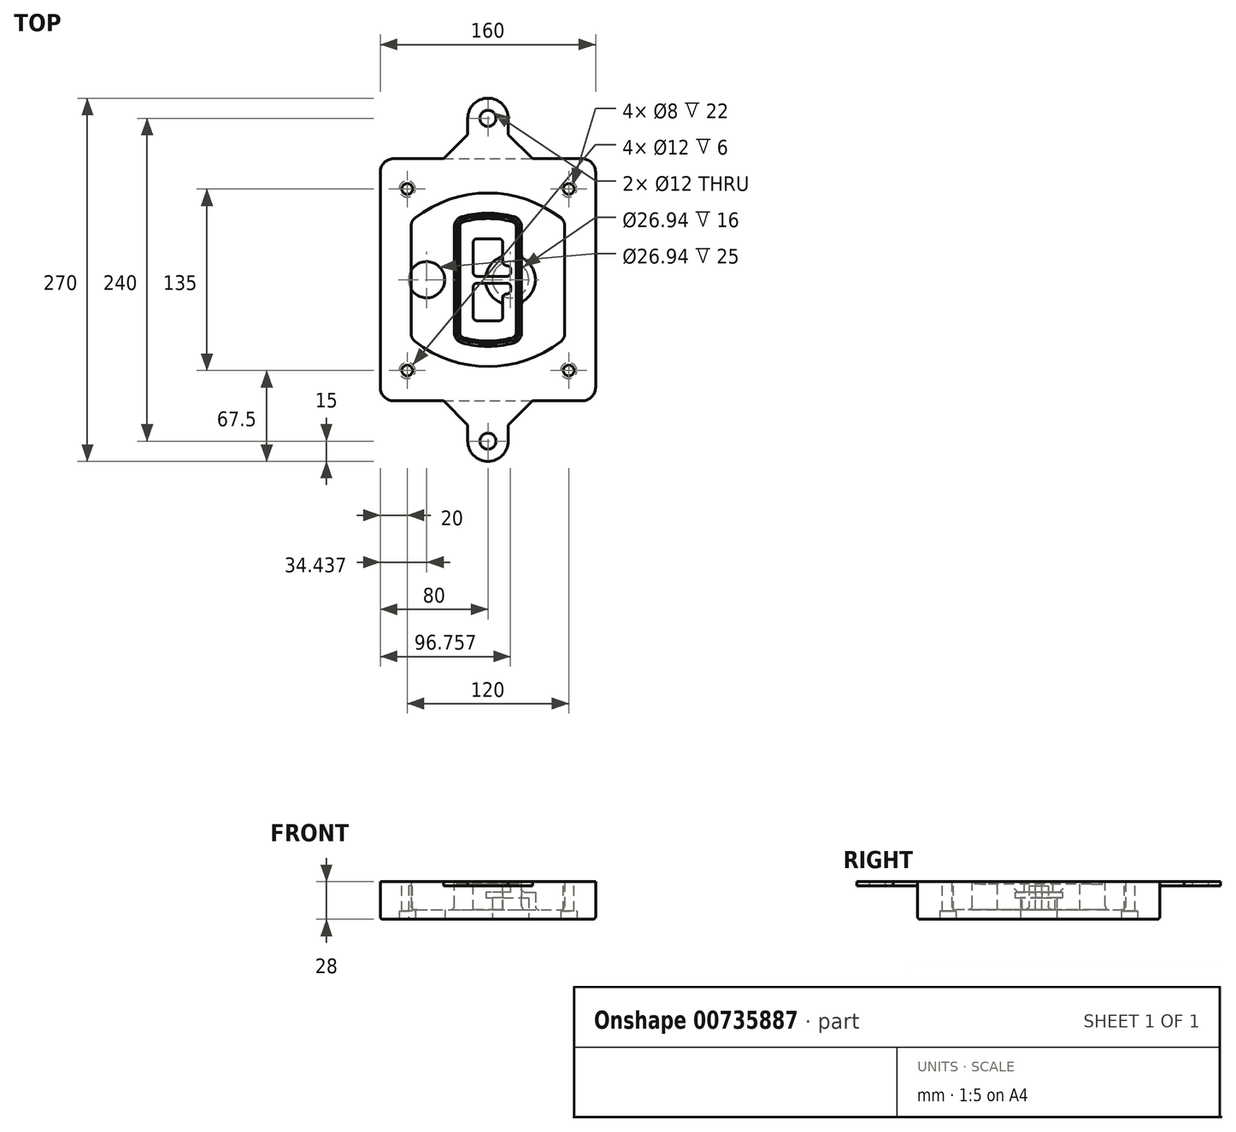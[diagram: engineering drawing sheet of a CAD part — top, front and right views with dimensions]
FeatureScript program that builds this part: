
annotation { "Feature Type Name" : "Feature", "Feature Type Description" : "" }
export const myFeature = defineFeature(function(context is Context, id is Id, definition is map)
    precondition{}
    {
        {
            var Q0;
            Q0=qCreatedBy(makeId("Top.planeOp"),FACE);
            var sketch = newSketch(context, id + "F0", { "sketchPlane" : qUnion([Q0])});
            skPoint(sketch, "E0.rect.middle", {"position": v(0, 0) * mm});
            skLineSegment(sketch, "E1.bottom", {"start": v(-70, -90) * mm, "end": v(70, -90) * mm});
            skLineSegment(sketch, "E1.top", {"start": v(-70, 90) * mm, "end": v(70, 90) * mm});
            skLineSegment(sketch, "E1.left", {"start": v(-80, -80) * mm, "end": v(-80, 80) * mm});
            skLineSegment(sketch, "E1.right", {"start": v(80, -80) * mm, "end": v(80, 80) * mm});
            skLineSegment(sketch, "E2", {"start": v(-80, 90) * mm, "end": v(80, -90) * mm, "construction": true});
            skLineSegment(sketch, "E3", {"start": v(80, 90) * mm, "end": v(-80, -90) * mm, "construction": true});
            skCircle(sketch, "E4", {"center": v(-60, 67.5) * mm, "radius": 4 * mm});
            skCircle(sketch, "E5", {"center": v(60, 67.5) * mm, "radius": 4 * mm});
            skCircle(sketch, "E6", {"center": v(60, -67.5) * mm, "radius": 4 * mm});
            skCircle(sketch, "E7", {"center": v(-60, -67.5) * mm, "radius": 4 * mm});
            skLineSegment(sketch, "E8", {"start": v(-60, 67.5) * mm, "end": v(60, 67.5) * mm, "construction": true});
            skLineSegment(sketch, "E9", {"start": v(60, 67.5) * mm, "end": v(60, -67.5) * mm, "construction": true});
            skLineSegment(sketch, "E10", {"start": v(60, -67.5) * mm, "end": v(-60, -67.5) * mm, "construction": true});
            skLineSegment(sketch, "E11", {"start": v(-60, -67.5) * mm, "end": v(-60, 67.5) * mm, "construction": true});
            skLineSegment(sketch, "E12", {"start": v(-60, 40.3) * mm, "end": v(-60, -40.3) * mm});
            skLineSegment(sketch, "E13", {"start": v(60, 40.3) * mm, "end": v(60, -40.3) * mm});
            skArc(sketch, "E14", {"start": v(56.15, 48.18) * mm, "mid": v(0, 67.5) * mm, "end": v(-56.15, 48.18) * mm});
            skArc(sketch, "E15", {"start": v(-56.15, -48.18) * mm, "mid": v(0, -67.5) * mm, "end": v(56.15, -48.18) * mm});
            skLineSegment(sketch, "E16", {"start": v(-60, 0) * mm, "end": v(60, 0) * mm, "construction": true});
            skPoint(sketch, "E17.visualSharp", {"position": v(-60, -45) * mm});
            skArc(sketch, "E17.filletArc", {"start": v(-60, -40.3) * mm, "mid": v(-58.99, -44.68) * mm, "end": v(-56.15, -48.18) * mm});
            skPoint(sketch, "E18.visualSharp", {"position": v(-60, 45) * mm});
            skArc(sketch, "E18.filletArc", {"start": v(-56.15, 48.18) * mm, "mid": v(-58.99, 44.68) * mm, "end": v(-60, 40.3) * mm});
            skPoint(sketch, "E19.visualSharp", {"position": v(60, 45) * mm});
            skArc(sketch, "E19.filletArc", {"start": v(60, 40.3) * mm, "mid": v(58.99, 44.68) * mm, "end": v(56.15, 48.18) * mm});
            skPoint(sketch, "E20.visualSharp", {"position": v(60, -45) * mm});
            skArc(sketch, "E20.filletArc", {"start": v(56.15, -48.18) * mm, "mid": v(58.99, -44.68) * mm, "end": v(60, -40.3) * mm});
            skPoint(sketch, "E21.visualSharp", {"position": v(-80, 90) * mm});
            skArc(sketch, "E21.filletArc", {"start": v(-70, 90) * mm, "mid": v(-77.07, 87.07) * mm, "end": v(-80, 80) * mm});
            skPoint(sketch, "E22.visualSharp", {"position": v(80, 90) * mm});
            skArc(sketch, "E22.filletArc", {"start": v(80, 80) * mm, "mid": v(77.07, 87.07) * mm, "end": v(70, 90) * mm});
            skPoint(sketch, "E23.visualSharp", {"position": v(80, -90) * mm});
            skArc(sketch, "E23.filletArc", {"start": v(70, -90) * mm, "mid": v(77.07, -87.07) * mm, "end": v(80, -80) * mm});
            skPoint(sketch, "E24.visualSharp", {"position": v(-80, -90) * mm});
            skArc(sketch, "E24.filletArc", {"start": v(-80, -80) * mm, "mid": v(-77.07, -87.07) * mm, "end": v(-70, -90) * mm});
            skArc(sketch, "E25.0", {"start": v(57, 40.3) * mm, "mid": v(56.3, 43.36) * mm, "end": v(54.3, 45.81) * mm});
            skLineSegment(sketch, "E25.1", {"start": v(57, 40.3) * mm, "end": v(57, -40.3) * mm});
            skArc(sketch, "E25.2", {"start": v(54.3, -45.81) * mm, "mid": v(56.3, -43.36) * mm, "end": v(57, -40.3) * mm});
            skArc(sketch, "E25.3", {"start": v(-54.3, -45.81) * mm, "mid": v(0, -64.5) * mm, "end": v(54.3, -45.81) * mm});
            skArc(sketch, "E25.4", {"start": v(-57, -40.3) * mm, "mid": v(-56.3, -43.36) * mm, "end": v(-54.3, -45.81) * mm});
            skArc(sketch, "E25.5", {"start": v(54.3, 45.81) * mm, "mid": v(0, 64.5) * mm, "end": v(-54.3, 45.81) * mm});
            skLineSegment(sketch, "E25.6", {"start": v(-57, 40.3) * mm, "end": v(-57, -40.3) * mm});
            skArc(sketch, "E25.7", {"start": v(-54.3, 45.81) * mm, "mid": v(-56.3, 43.36) * mm, "end": v(-57, 40.3) * mm});
            skArc(sketch, "E26.0", {"start": v(-58.62, 51.33) * mm, "mid": v(-62.58, 46.43) * mm, "end": v(-64, 40.3) * mm});
            skArc(sketch, "E26.1", {"start": v(58.62, 51.33) * mm, "mid": v(0, 71.5) * mm, "end": v(-58.62, 51.33) * mm});
            skArc(sketch, "E26.2", {"start": v(64, 40.3) * mm, "mid": v(62.58, 46.43) * mm, "end": v(58.62, 51.33) * mm});
            skLineSegment(sketch, "E26.3", {"start": v(64, 40.3) * mm, "end": v(64, -40.3) * mm});
            skArc(sketch, "E26.4", {"start": v(58.62, -51.33) * mm, "mid": v(62.58, -46.43) * mm, "end": v(64, -40.3) * mm});
            skLineSegment(sketch, "E26.5", {"start": v(-64, 40.3) * mm, "end": v(-64, -40.3) * mm});
            skArc(sketch, "E26.6", {"start": v(-58.62, -51.33) * mm, "mid": v(0, -71.5) * mm, "end": v(58.62, -51.33) * mm});
            skArc(sketch, "E26.7", {"start": v(-64, -40.3) * mm, "mid": v(-62.58, -46.43) * mm, "end": v(-58.62, -51.33) * mm});
            skSolve(sketch);
        }
        {
            var Q0;
            Q0=makeQuery(id+"F0.imprint","IMPRINT",FACE,{"disambiguationData":[TD([[makeQuery(id+"F0.imprint","IMPRINT",EDGE,{"derivedFrom":sQuery(id+"F0.wireOp",EDGE,"E1.bottom")}),1.0]])]});
            var Q1;
            Q1=makeQuery(id+"F0.imprint","IMPRINT",FACE,{"disambiguationData":[TD([[makeQuery(id+"F0.imprint","IMPRINT",EDGE,{"derivedFrom":sQuery(id+"F0.wireOp",EDGE,"E12")}),1.0]])]});
            var Q2;
            Q2=makeQuery(id+"F0.imprint","IMPRINT",FACE,{"disambiguationData":[TD([[makeQuery(id+"F0.imprint","IMPRINT",EDGE,{"derivedFrom":sQuery(id+"F0.wireOp",EDGE,"E25.0")}),1.0]])]});
            var Q3;
            Q3=makeQuery(id+"F0.imprint","IMPRINT",FACE,{"disambiguationData":[TD([[makeQuery(id+"F0.imprint","IMPRINT",EDGE,{"derivedFrom":sQuery(id+"F0.wireOp",EDGE,"E12")}),-1.0]])]});
            extrude(context, id + "F1", {"entities" : qUnion([Q0, Q1, Q2, Q3]), "oppositeDirection" : true, "depth" : 25 * mm});
        }
        {
            var Q0;
            Q0=makeQuery(id+"F0.imprint","IMPRINT",FACE,{"disambiguationData":[TD([[makeQuery(id+"F0.imprint","IMPRINT",EDGE,{"derivedFrom":sQuery(id+"F0.wireOp",EDGE,"E12")}),1.0]])]});
            extrude(context, id + "F2", {"entities" : qUnion([Q0]), "operationType" : NewBodyOperationType.ADD, "depth" : 3 * mm});
        }
        {
            var Q0;
            Q0=makeQuery(id+"F0.imprint","IMPRINT",FACE,{"disambiguationData":[TD([[makeQuery(id+"F0.imprint","IMPRINT",EDGE,{"derivedFrom":sQuery(id+"F0.wireOp",EDGE,"E25.0")}),1.0]])]});
            extrude(context, id + "F3", {"entities" : qUnion([Q0]), "operationType" : NewBodyOperationType.REMOVE, "oppositeDirection" : true, "depth" : 18 * mm});
        }
        {
            var Q0;
            Q0=makeQuery(id+"F2.opExtrude","CAP_FACE",FACE,{"disambiguationData":[OSD([sQuery(id+"F0.wireOp",EDGE,"E12"),sQuery(id+"F0.wireOp",EDGE,"E13"),sQuery(id+"F0.wireOp",EDGE,"E14"),sQuery(id+"F0.wireOp",EDGE,"E15"),sQuery(id+"F0.wireOp",EDGE,"E17.filletArc"),sQuery(id+"F0.wireOp",EDGE,"E18.filletArc"),sQuery(id+"F0.wireOp",EDGE,"E19.filletArc"),sQuery(id+"F0.wireOp",EDGE,"E20.filletArc"),sQuery(id+"F0.wireOp",EDGE,"E25.0"),sQuery(id+"F0.wireOp",EDGE,"E25.1"),sQuery(id+"F0.wireOp",EDGE,"E25.2"),sQuery(id+"F0.wireOp",EDGE,"E25.3"),sQuery(id+"F0.wireOp",EDGE,"E25.4"),sQuery(id+"F0.wireOp",EDGE,"E25.5"),sQuery(id+"F0.wireOp",EDGE,"E25.6"),sQuery(id+"F0.wireOp",EDGE,"E25.7")])],"isStart":false});
            var sketch = newSketch(context, id + "F4", { "sketchPlane" : qUnion([Q0])});
            skArc(sketch, "E27.0", {"start": v(-19.08, -46.97) * mm, "mid": v(0, -49.5) * mm, "end": v(19.08, -46.97) * mm});
            skArc(sketch, "E28.0", {"start": v(19.08, 46.97) * mm, "mid": v(0, 49.5) * mm, "end": v(-19.08, 46.97) * mm});
            skLineSegment(sketch, "E29", {"start": v(-25, 39.25) * mm, "end": v(-25, -39.25) * mm});
            skLineSegment(sketch, "E30", {"start": v(25, 39.25) * mm, "end": v(25, -39.25) * mm});
            skLineSegment(sketch, "E31", {"start": v(-25, 45.1) * mm, "end": v(25, 45.1) * mm, "construction": true});
            skLineSegment(sketch, "E32", {"start": v(-25, -45.1) * mm, "end": v(25, -45.1) * mm, "construction": true});
            skPoint(sketch, "E33.visualSharp", {"position": v(-25, 45.1) * mm});
            skArc(sketch, "E33.filletArc", {"start": v(-19.08, 46.97) * mm, "mid": v(-23.35, 44.11) * mm, "end": v(-25, 39.25) * mm});
            skPoint(sketch, "E34.visualSharp", {"position": v(25, 45.1) * mm});
            skArc(sketch, "E34.filletArc", {"start": v(25, 39.25) * mm, "mid": v(23.35, 44.11) * mm, "end": v(19.08, 46.97) * mm});
            skPoint(sketch, "E35.visualSharp", {"position": v(25, -45.1) * mm});
            skArc(sketch, "E35.filletArc", {"start": v(19.08, -46.97) * mm, "mid": v(23.35, -44.11) * mm, "end": v(25, -39.25) * mm});
            skPoint(sketch, "E36.visualSharp", {"position": v(-25, -45.1) * mm});
            skArc(sketch, "E36.filletArc", {"start": v(-25, -39.25) * mm, "mid": v(-23.35, -44.11) * mm, "end": v(-19.08, -46.97) * mm});
            skArc(sketch, "E37.0", {"start": v(54.3, 45.81) * mm, "mid": v(0, 64.5) * mm, "end": v(-54.3, 45.81) * mm});
            skArc(sketch, "E37.1", {"start": v(-54.3, 45.81) * mm, "mid": v(-56.3, 43.36) * mm, "end": v(-57, 40.3) * mm});
            skLineSegment(sketch, "E37.2", {"start": v(-57, 40.3) * mm, "end": v(-57, -40.3) * mm});
            skArc(sketch, "E37.3", {"start": v(-57, -40.3) * mm, "mid": v(-56.3, -43.36) * mm, "end": v(-54.3, -45.81) * mm});
            skArc(sketch, "E37.4", {"start": v(-54.3, -45.81) * mm, "mid": v(0, -64.5) * mm, "end": v(54.3, -45.81) * mm});
            skArc(sketch, "E37.5", {"start": v(54.3, -45.81) * mm, "mid": v(56.3, -43.36) * mm, "end": v(57, -40.3) * mm});
            skLineSegment(sketch, "E37.6", {"start": v(57, 40.3) * mm, "end": v(57, -40.3) * mm});
            skArc(sketch, "E37.7", {"start": v(57, 40.3) * mm, "mid": v(56.3, 43.36) * mm, "end": v(54.3, 45.81) * mm});
            skLineSegment(sketch, "E38.0", {"start": v(23, 39.25) * mm, "end": v(23, -39.25) * mm});
            skArc(sketch, "E38.1", {"start": v(18.56, -45.04) * mm, "mid": v(21.76, -42.9) * mm, "end": v(23, -39.25) * mm});
            skArc(sketch, "E38.2", {"start": v(-18.56, -45.04) * mm, "mid": v(0, -47.5) * mm, "end": v(18.56, -45.04) * mm});
            skArc(sketch, "E38.3", {"start": v(-23, -39.25) * mm, "mid": v(-21.76, -42.9) * mm, "end": v(-18.56, -45.04) * mm});
            skLineSegment(sketch, "E38.4", {"start": v(-23, 39.25) * mm, "end": v(-23, -39.25) * mm});
            skArc(sketch, "E38.5", {"start": v(23, 39.25) * mm, "mid": v(21.76, 42.9) * mm, "end": v(18.56, 45.04) * mm});
            skArc(sketch, "E38.6", {"start": v(-18.56, 45.04) * mm, "mid": v(-21.76, 42.9) * mm, "end": v(-23, 39.25) * mm});
            skArc(sketch, "E38.7", {"start": v(18.56, 45.04) * mm, "mid": v(0, 47.5) * mm, "end": v(-18.56, 45.04) * mm});
            skArc(sketch, "E39.0", {"start": v(21, 39.25) * mm, "mid": v(20.18, 41.68) * mm, "end": v(18.04, 43.1) * mm});
            skLineSegment(sketch, "E39.1", {"start": v(21, 39.25) * mm, "end": v(21, -39.25) * mm});
            skArc(sketch, "E39.2", {"start": v(18.04, -43.1) * mm, "mid": v(20.18, -41.68) * mm, "end": v(21, -39.25) * mm});
            skArc(sketch, "E39.3", {"start": v(-18.04, -43.1) * mm, "mid": v(0, -45.5) * mm, "end": v(18.04, -43.1) * mm});
            skArc(sketch, "E39.4", {"start": v(-21, -39.25) * mm, "mid": v(-20.18, -41.68) * mm, "end": v(-18.04, -43.1) * mm});
            skArc(sketch, "E39.5", {"start": v(18.04, 43.1) * mm, "mid": v(0, 45.5) * mm, "end": v(-18.04, 43.1) * mm});
            skLineSegment(sketch, "E39.6", {"start": v(-21, 39.25) * mm, "end": v(-21, -39.25) * mm});
            skArc(sketch, "E39.7", {"start": v(-18.04, 43.1) * mm, "mid": v(-20.18, 41.68) * mm, "end": v(-21, 39.25) * mm});
            skLineSegment(sketch, "E40", {"start": v(-25, 0) * mm, "end": v(25, 0) * mm, "construction": true});
            skLineSegment(sketch, "E41", {"start": v(-11, 5.5) * mm, "end": v(-11, 27.5) * mm});
            skLineSegment(sketch, "E42", {"start": v(-8, 30.5) * mm, "end": v(8, 30.5) * mm});
            skLineSegment(sketch, "E43", {"start": v(11, 27.5) * mm, "end": v(11, 13.5) * mm});
            skLineSegment(sketch, "E44", {"start": v(14, 10.5) * mm, "end": v(14, 10.5) * mm});
            skLineSegment(sketch, "E45", {"start": v(17, 7.5) * mm, "end": v(17, 5.5) * mm});
            skLineSegment(sketch, "E46", {"start": v(14, 2.5) * mm, "end": v(-8, 2.5) * mm});
            skPoint(sketch, "E47.visualSharp", {"position": v(-11, 30.5) * mm});
            skArc(sketch, "E47.filletArc", {"start": v(-8, 30.5) * mm, "mid": v(-10.12, 29.62) * mm, "end": v(-11, 27.5) * mm});
            skPoint(sketch, "E48.visualSharp", {"position": v(11, 30.5) * mm});
            skArc(sketch, "E48.filletArc", {"start": v(11, 27.5) * mm, "mid": v(10.12, 29.62) * mm, "end": v(8, 30.5) * mm});
            skPoint(sketch, "E49.visualSharp", {"position": v(11, 10.5) * mm});
            skArc(sketch, "E49.filletArc", {"start": v(11, 13.5) * mm, "mid": v(11.88, 11.38) * mm, "end": v(14, 10.5) * mm});
            skPoint(sketch, "E50.visualSharp", {"position": v(17, 10.5) * mm});
            skArc(sketch, "E50.filletArc", {"start": v(17, 7.5) * mm, "mid": v(16.12, 9.62) * mm, "end": v(14, 10.5) * mm});
            skPoint(sketch, "E51.visualSharp", {"position": v(17, 2.5) * mm});
            skArc(sketch, "E51.filletArc", {"start": v(14, 2.5) * mm, "mid": v(16.12, 3.38) * mm, "end": v(17, 5.5) * mm});
            skPoint(sketch, "E52.visualSharp", {"position": v(-11, 2.5) * mm});
            skArc(sketch, "E52.filletArc", {"start": v(-11, 5.5) * mm, "mid": v(-10.12, 3.38) * mm, "end": v(-8, 2.5) * mm});
            skLineSegment(sketch, "E53.0.MirrorCS", {"start": v(14, -2.5) * mm, "end": v(-8, -2.5) * mm});
            skArc(sketch, "E54.0.MirrorCS", {"start": v(-11, -5.5) * mm, "mid": v(-10.12, -3.38) * mm, "end": v(-8, -2.5) * mm});
            skLineSegment(sketch, "E55.0.MirrorCS", {"start": v(-11, -5.5) * mm, "end": v(-11, -27.5) * mm});
            skArc(sketch, "E56.0.MirrorCS", {"start": v(-8, -30.5) * mm, "mid": v(-10.12, -29.62) * mm, "end": v(-11, -27.5) * mm});
            skLineSegment(sketch, "E57.0.MirrorCS", {"start": v(-8, -30.5) * mm, "end": v(8, -30.5) * mm});
            skArc(sketch, "E58.0.MirrorCS", {"start": v(11, -27.5) * mm, "mid": v(10.12, -29.62) * mm, "end": v(8, -30.5) * mm});
            skLineSegment(sketch, "E59.0.MirrorCS", {"start": v(11, -27.5) * mm, "end": v(11, -13.5) * mm});
            skArc(sketch, "E60.0.MirrorCS", {"start": v(11, -13.5) * mm, "mid": v(11.88, -11.38) * mm, "end": v(14, -10.5) * mm});
            skArc(sketch, "E61.0.MirrorCS", {"start": v(17, -7.5) * mm, "mid": v(16.12, -9.62) * mm, "end": v(14, -10.5) * mm});
            skLineSegment(sketch, "E62.0.MirrorCS", {"start": v(17, -7.5) * mm, "end": v(17, -5.5) * mm});
            skArc(sketch, "E63.0.MirrorCS", {"start": v(14, -2.5) * mm, "mid": v(16.12, -3.38) * mm, "end": v(17, -5.5) * mm});
            skSolve(sketch);
        }
        {
            var Q0;
            Q0=makeQuery(id+"F4.imprint","IMPRINT",FACE,{"disambiguationData":[TD([[makeQuery(id+"F4.imprint","IMPRINT",EDGE,{"derivedFrom":sQuery(id+"F4.wireOp",EDGE,"E27.0")}),1.0]])]});
            var Q1;
            Q1=makeQuery(id+"F4.imprint","IMPRINT",FACE,{"disambiguationData":[TD([[makeQuery(id+"F4.imprint","IMPRINT",EDGE,{"derivedFrom":sQuery(id+"F4.wireOp",EDGE,"E38.0")}),-1.0]])]});
            var Q2;
            Q2=makeQuery(id+"F4.imprint","IMPRINT",FACE,{"disambiguationData":[TD([[makeQuery(id+"F4.imprint","IMPRINT",EDGE,{"derivedFrom":sQuery(id+"F4.wireOp",EDGE,"E39.0")}),1.0]])]});
            extrude(context, id + "F5", {"entities" : qUnion([Q0, Q1, Q2]), "operationType" : NewBodyOperationType.ADD, "endBound" : BoundingType.UP_TO_NEXT, "oppositeDirection" : true, "depth" : 25 * mm});
        }
        {
            var Q0;
            Q0=makeQuery(id+"F4.imprint","IMPRINT",FACE,{"disambiguationData":[TD([[makeQuery(id+"F4.imprint","IMPRINT",EDGE,{"derivedFrom":sQuery(id+"F4.wireOp",EDGE,"E38.0")}),-1.0]])]});
            extrude(context, id + "F6", {"entities" : qUnion([Q0]), "operationType" : NewBodyOperationType.REMOVE, "oppositeDirection" : true, "depth" : 2 * mm});
        }
        {
            var Q0;
            Q0=makeQuery(id+"F1.opExtrude","CAP_FACE",FACE,{"disambiguationData":[OSD([sQuery(id+"F0.wireOp",EDGE,"E1.bottom"),sQuery(id+"F0.wireOp",EDGE,"E1.top"),sQuery(id+"F0.wireOp",EDGE,"E1.left"),sQuery(id+"F0.wireOp",EDGE,"E1.right"),sQuery(id+"F0.wireOp",EDGE,"E4"),sQuery(id+"F0.wireOp",EDGE,"E5"),sQuery(id+"F0.wireOp",EDGE,"E6"),sQuery(id+"F0.wireOp",EDGE,"E7"),sQuery(id+"F0.wireOp",EDGE,"E21.filletArc"),sQuery(id+"F0.wireOp",EDGE,"E22.filletArc"),sQuery(id+"F0.wireOp",EDGE,"E23.filletArc"),sQuery(id+"F0.wireOp",EDGE,"E24.filletArc")])],"isStart":false});
            var sketch = newSketch(context, id + "F7", { "sketchPlane" : qUnion([Q0])});
            skCircle(sketch, "E64", {"center": v(16.76, 0) * mm, "radius": 13.47 * mm});
            skCircle(sketch, "E65", {"center": v(-45.56, 0) * mm, "radius": 13.47 * mm});
            skLineSegment(sketch, "E66", {"start": v(80, 0) * mm, "end": v(-80, 0) * mm});
            skCircle(sketch, "E67", {"center": v(16.76, 0) * mm, "radius": 18.47 * mm});
            skCircle(sketch, "E68", {"center": v(60, -67.5) * mm, "radius": 6 * mm});
            skCircle(sketch, "E69", {"center": v(-60, -67.5) * mm, "radius": 6 * mm});
            skCircle(sketch, "E70", {"center": v(-60, 67.5) * mm, "radius": 6 * mm});
            skCircle(sketch, "E71", {"center": v(60, 67.5) * mm, "radius": 6 * mm});
            skSolve(sketch);
        }
        {
            var Q0;
            {var subQ1=sQuery(id+"F7.wireOp",EDGE,"E66");var subQ4=sQuery(id+"F7.wireOp",EDGE,"E64");var subQ6=makeQuery(id+"F7.imprint","INTERSECT",VERTEX,{"disambiguationData":[OD(0.0)],"derivedFrom":[subQ4,subQ1]});Q0=makeQuery(id+"F7.imprint","IMPRINT",FACE,{"disambiguationData":[TD([[makeQuery(id+"F7.imprint","IMPRINT",EDGE,{"disambiguationData":[TD([[subQ6,-1.0]])],"derivedFrom":subQ4}),-1.0]])]});}
            var Q1;
            {var subQ0=sQuery(id+"F7.wireOp",EDGE,"E66");var subQ1=sQuery(id+"F7.wireOp",EDGE,"E64");var subQ3=makeQuery(id+"F7.imprint","INTERSECT",VERTEX,{"disambiguationData":[OD(0.0)],"derivedFrom":[subQ1,subQ0]});Q1=makeQuery(id+"F7.imprint","IMPRINT",FACE,{"disambiguationData":[TD([[makeQuery(id+"F7.imprint","IMPRINT",EDGE,{"disambiguationData":[TD([[subQ3,-1.0]])],"derivedFrom":subQ1}),1.0]])]});}
            var Q2;
            {var subQ0=sQuery(id+"F7.wireOp",EDGE,"E66");var subQ1=sQuery(id+"F7.wireOp",EDGE,"E64");var subQ3=makeQuery(id+"F7.imprint","INTERSECT",VERTEX,{"disambiguationData":[OD(0.0)],"derivedFrom":[subQ1,subQ0]});Q2=makeQuery(id+"F7.imprint","IMPRINT",FACE,{"disambiguationData":[TD([[makeQuery(id+"F7.imprint","IMPRINT",EDGE,{"disambiguationData":[TD([[subQ3,1.0]])],"derivedFrom":subQ1}),1.0]])]});}
            var Q3;
            {var subQ1=sQuery(id+"F7.wireOp",EDGE,"E66");var subQ4=sQuery(id+"F7.wireOp",EDGE,"E64");var subQ6=makeQuery(id+"F7.imprint","INTERSECT",VERTEX,{"disambiguationData":[OD(0.0)],"derivedFrom":[subQ4,subQ1]});Q3=makeQuery(id+"F7.imprint","IMPRINT",FACE,{"disambiguationData":[TD([[makeQuery(id+"F7.imprint","IMPRINT",EDGE,{"disambiguationData":[TD([[subQ6,1.0]])],"derivedFrom":subQ4}),-1.0]])]});}
            extrude(context, id + "F8", {"entities" : qUnion([Q0, Q1, Q2, Q3]), "operationType" : NewBodyOperationType.ADD, "oppositeDirection" : true, "depth" : 20 * mm});
        }
        {
            var Q0;
            {var subQ0=sQuery(id+"F7.wireOp",EDGE,"E66");var subQ1=sQuery(id+"F7.wireOp",EDGE,"E64");var subQ3=makeQuery(id+"F7.imprint","INTERSECT",VERTEX,{"disambiguationData":[OD(0.0)],"derivedFrom":[subQ1,subQ0]});Q0=makeQuery(id+"F7.imprint","IMPRINT",FACE,{"disambiguationData":[TD([[makeQuery(id+"F7.imprint","IMPRINT",EDGE,{"disambiguationData":[TD([[subQ3,-1.0]])],"derivedFrom":subQ1}),1.0]])]});}
            var Q1;
            {var subQ0=sQuery(id+"F7.wireOp",EDGE,"E66");var subQ1=sQuery(id+"F7.wireOp",EDGE,"E64");var subQ3=makeQuery(id+"F7.imprint","INTERSECT",VERTEX,{"disambiguationData":[OD(0.0)],"derivedFrom":[subQ1,subQ0]});Q1=makeQuery(id+"F7.imprint","IMPRINT",FACE,{"disambiguationData":[TD([[makeQuery(id+"F7.imprint","IMPRINT",EDGE,{"disambiguationData":[TD([[subQ3,1.0]])],"derivedFrom":subQ1}),1.0]])]});}
            extrude(context, id + "F9", {"entities" : qUnion([Q0, Q1]), "operationType" : NewBodyOperationType.REMOVE, "oppositeDirection" : true, "depth" : 16 * mm});
        }
        {
            var Q0;
            {var subQ0=sQuery(id+"F7.wireOp",EDGE,"E66");var subQ1=sQuery(id+"F7.wireOp",EDGE,"E65");var subQ3=makeQuery(id+"F7.imprint","INTERSECT",VERTEX,{"disambiguationData":[OD(0.0)],"derivedFrom":[subQ1,subQ0]});Q0=makeQuery(id+"F7.imprint","IMPRINT",FACE,{"disambiguationData":[TD([[makeQuery(id+"F7.imprint","IMPRINT",EDGE,{"disambiguationData":[TD([[subQ3,-1.0]])],"derivedFrom":subQ1}),1.0]])]});}
            var Q1;
            {var subQ0=sQuery(id+"F7.wireOp",EDGE,"E66");var subQ1=sQuery(id+"F7.wireOp",EDGE,"E65");var subQ3=makeQuery(id+"F7.imprint","INTERSECT",VERTEX,{"disambiguationData":[OD(0.0)],"derivedFrom":[subQ1,subQ0]});Q1=makeQuery(id+"F7.imprint","IMPRINT",FACE,{"disambiguationData":[TD([[makeQuery(id+"F7.imprint","IMPRINT",EDGE,{"disambiguationData":[TD([[subQ3,1.0]])],"derivedFrom":subQ1}),1.0]])]});}
            extrude(context, id + "F10", {"entities" : qUnion([Q0, Q1]), "operationType" : NewBodyOperationType.REMOVE, "oppositeDirection" : true, "depth" : 25 * mm});
        }
        {
            var Q0;
            Q0=makeQuery(id+"F7.imprint","IMPRINT",FACE,{"disambiguationData":[TD([[makeQuery(id+"F7.imprint","IMPRINT",EDGE,{"derivedFrom":sQuery(id+"F7.wireOp",EDGE,"E68")}),1.0]])]});
            var Q1;
            Q1=makeQuery(id+"F7.imprint","IMPRINT",FACE,{"disambiguationData":[TD([[makeQuery(id+"F7.imprint","IMPRINT",EDGE,{"derivedFrom":makeQuery(id+"F1.opExtrude","CAP_EDGE",EDGE,{"disambiguationData":[OSD([sQuery(id+"F0.wireOp",EDGE,"E5")])],"isStart":false})}),-1.0]])]});
            var Q2;
            Q2=makeQuery(id+"F7.imprint","IMPRINT",FACE,{"disambiguationData":[TD([[makeQuery(id+"F7.imprint","IMPRINT",EDGE,{"derivedFrom":sQuery(id+"F7.wireOp",EDGE,"E69")}),1.0]])]});
            var Q3;
            Q3=makeQuery(id+"F7.imprint","IMPRINT",FACE,{"disambiguationData":[TD([[makeQuery(id+"F7.imprint","IMPRINT",EDGE,{"derivedFrom":makeQuery(id+"F1.opExtrude","CAP_EDGE",EDGE,{"disambiguationData":[OSD([sQuery(id+"F0.wireOp",EDGE,"E4")])],"isStart":false})}),-1.0]])]});
            var Q4;
            Q4=makeQuery(id+"F7.imprint","IMPRINT",FACE,{"disambiguationData":[TD([[makeQuery(id+"F7.imprint","IMPRINT",EDGE,{"derivedFrom":sQuery(id+"F7.wireOp",EDGE,"E70")}),1.0]])]});
            var Q5;
            Q5=makeQuery(id+"F7.imprint","IMPRINT",FACE,{"disambiguationData":[TD([[makeQuery(id+"F7.imprint","IMPRINT",EDGE,{"derivedFrom":makeQuery(id+"F1.opExtrude","CAP_EDGE",EDGE,{"disambiguationData":[OSD([sQuery(id+"F0.wireOp",EDGE,"E7")])],"isStart":false})}),-1.0]])]});
            var Q6;
            Q6=makeQuery(id+"F7.imprint","IMPRINT",FACE,{"disambiguationData":[TD([[makeQuery(id+"F7.imprint","IMPRINT",EDGE,{"derivedFrom":sQuery(id+"F7.wireOp",EDGE,"E71")}),1.0]])]});
            var Q7;
            Q7=makeQuery(id+"F7.imprint","IMPRINT",FACE,{"disambiguationData":[TD([[makeQuery(id+"F7.imprint","IMPRINT",EDGE,{"derivedFrom":makeQuery(id+"F1.opExtrude","CAP_EDGE",EDGE,{"disambiguationData":[OSD([sQuery(id+"F0.wireOp",EDGE,"E6")])],"isStart":false})}),-1.0]])]});
            extrude(context, id + "F11", {"entities" : qUnion([Q0, Q1, Q2, Q3, Q4, Q5, Q6, Q7]), "operationType" : NewBodyOperationType.REMOVE, "oppositeDirection" : true, "depth" : 6 * mm});
        }
        {
            var Q0;
            Q0=makeQuery(id+"F9.boolean.opBoolean","COPY",FACE,{"derivedFrom":makeQuery(id+"F9.opExtrude","CAP_FACE",FACE,{"disambiguationData":[OSD([sQuery(id+"F7.wireOp",EDGE,"E64")])],"isStart":false})});
            var sketch = newSketch(context, id + "F12", { "sketchPlane" : qUnion([Q0])});
            skArc(sketch, "E72.0", {"start": v(11, 17.55) * mm, "mid": v(2.57, 11.82) * mm, "end": v(-1.54, 2.5) * mm});
            skArc(sketch, "E72.1", {"start": v(-1.54, -2.5) * mm, "mid": v(2.57, -11.82) * mm, "end": v(11, -17.55) * mm});
            skLineSegment(sketch, "E73", {"start": v(-1.54, -2.5) * mm, "end": v(14, -2.5) * mm});
            skLineSegment(sketch, "E74.0", {"start": v(14, 2.5) * mm, "end": v(-1.54, 2.5) * mm});
            skArc(sketch, "E74.1", {"start": v(14, 2.5) * mm, "mid": v(16.12, 3.38) * mm, "end": v(17, 5.5) * mm});
            skLineSegment(sketch, "E74.2", {"start": v(17, 7.5) * mm, "end": v(17, 5.5) * mm});
            skArc(sketch, "E74.3", {"start": v(17, 7.5) * mm, "mid": v(16.12, 9.62) * mm, "end": v(14, 10.5) * mm});
            skArc(sketch, "E74.4", {"start": v(11, 13.5) * mm, "mid": v(11.88, 11.38) * mm, "end": v(14, 10.5) * mm});
            skLineSegment(sketch, "E74.5", {"start": v(11, 17.55) * mm, "end": v(11, 13.5) * mm});
            skLineSegment(sketch, "E74.7", {"start": v(14, -2.5) * mm, "end": v(-1.54, -2.5) * mm});
            skArc(sketch, "E74.8", {"start": v(14, -2.5) * mm, "mid": v(16.12, -3.38) * mm, "end": v(17, -5.5) * mm});
            skLineSegment(sketch, "E74.9", {"start": v(17, -7.5) * mm, "end": v(17, -5.5) * mm});
            skArc(sketch, "E74.10", {"start": v(17, -7.5) * mm, "mid": v(16.12, -9.62) * mm, "end": v(14, -10.5) * mm});
            skArc(sketch, "E74.11", {"start": v(11, -13.5) * mm, "mid": v(11.88, -11.38) * mm, "end": v(14, -10.5) * mm});
            skLineSegment(sketch, "E74.12", {"start": v(11, -17.55) * mm, "end": v(11, -13.5) * mm});
            skPoint(sketch, "E75.orphan", {"position": v(11, -27.5) * mm});
            skPoint(sketch, "E76.orphan", {"position": v(-8, -2.5) * mm});
            skPoint(sketch, "E77.orphan", {"position": v(-8, 2.5) * mm});
            skPoint(sketch, "E78.orphan", {"position": v(11, 27.5) * mm});
            skSolve(sketch);
        }
        {
            var Q0;
            {var subQ7=sQuery(id+"F12.wireOp",EDGE,"E72.0");var subQ14=sQuery(id+"F12.wireOp",EDGE,"E72.1");var subQ16=sQuery(id+"F12.wireOp",EDGE,"E74.1");var subQ18=sQuery(id+"F12.wireOp",EDGE,"E74.8");Q0=qUnion([makeQuery(id+"F12.imprint","IMPRINT",FACE,{"disambiguationData":[TD([[makeQuery(id+"F12.imprint","IMPRINT",EDGE,{"derivedFrom":subQ7}),1.0]])]}),makeQuery(id+"F12.imprint","IMPRINT",FACE,{"disambiguationData":[TD([[makeQuery(id+"F12.imprint","IMPRINT",EDGE,{"derivedFrom":subQ14}),1.0]])]}),makeQuery(id+"F12.imprint","IMPRINT",FACE,{"disambiguationData":[TD([[makeQuery(id+"F12.imprint","IMPRINT",EDGE,{"derivedFrom":subQ16}),1.0]])]}),makeQuery(id+"F12.imprint","IMPRINT",FACE,{"disambiguationData":[TD([[makeQuery(id+"F12.imprint","IMPRINT",EDGE,{"derivedFrom":subQ18}),-1.0]])]})]);}
            var Q1;
            Q1=makeQuery(id+"F5.boolean.opBoolean","SPLIT",FACE,{"disambiguationData":[TD([makeQuery(id+"F5.opExtrude","SWEPT_FACE",FACE,{"disambiguationData":[OSD([sQuery(id+"F4.wireOp",EDGE,"E41")])]})])],"derivedFrom":makeQuery(id+"F3.boolean.opBoolean","COPY",FACE,{"derivedFrom":makeQuery(id+"F3.opExtrude","CAP_FACE",FACE,{"disambiguationData":[OSD([sQuery(id+"F0.wireOp",EDGE,"E25.0"),sQuery(id+"F0.wireOp",EDGE,"E25.1"),sQuery(id+"F0.wireOp",EDGE,"E25.2"),sQuery(id+"F0.wireOp",EDGE,"E25.3"),sQuery(id+"F0.wireOp",EDGE,"E25.4"),sQuery(id+"F0.wireOp",EDGE,"E25.5"),sQuery(id+"F0.wireOp",EDGE,"E25.6"),sQuery(id+"F0.wireOp",EDGE,"E25.7")])],"isStart":false})})});
            extrude(context, id + "F13", {"entities" : qUnion([Q0]), "operationType" : NewBodyOperationType.REMOVE, "endBound" : BoundingType.UP_TO_SURFACE, "endBoundEntityFace" : qUnion([Q1]), "depth" : 25 * mm});
        }
        {
            var Q0;
            Q0=makeQuery(id+"F3.boolean.opBoolean","COPY",EDGE,{"derivedFrom":makeQuery(id+"F3.opExtrude","CAP_EDGE",EDGE,{"disambiguationData":[OSD([sQuery(id+"F0.wireOp",EDGE,"E25.6")])],"isStart":false})});
            var Q1;
            Q1=makeQuery(id+"F8.boolean.opBoolean","INTERSECT",EDGE,{"derivedFrom":[makeQuery(id+"F5.opExtrude","SWEPT_FACE",FACE,{"disambiguationData":[OSD([sQuery(id+"F4.wireOp",EDGE,"E30")])]}),makeQuery(id+"F8.opExtrude","CAP_FACE",FACE,{"disambiguationData":[OSD([sQuery(id+"F7.wireOp",EDGE,"E67")])],"isStart":false})]});
            var Q2;
            Q2=makeQuery(id+"F8.boolean.opBoolean","INTERSECT",EDGE,{"disambiguationData":[OD(1.0)],"derivedFrom":[makeQuery(id+"F5.opExtrude","SWEPT_FACE",FACE,{"disambiguationData":[OSD([sQuery(id+"F4.wireOp",EDGE,"E30")])]}),makeQuery(id+"F8.opExtrude","SWEPT_FACE",FACE,{"disambiguationData":[OSD([sQuery(id+"F7.wireOp",EDGE,"E67")])]})]});
            var Q3;
            {var subQ0=sQuery(id+"F4.wireOp",EDGE,"E30");Q3=makeQuery(id+"F8.boolean.opBoolean","SPLIT",EDGE,{"disambiguationData":[TD([makeQuery(id+"F5.opExtrude","SWEPT_FACE",FACE,{"disambiguationData":[OSD([sQuery(id+"F4.wireOp",EDGE,"E35.filletArc")])]})])],"derivedFrom":makeQuery(id+"F5.opExtrude","CAP_EDGE",EDGE,{"disambiguationData":[OSD([subQ0])],"isStart":false})});}
            var Q4;
            {var subQ0=sQuery(id+"F0.wireOp",EDGE,"E25.7");var subQ1=sQuery(id+"F0.wireOp",EDGE,"E25.1");var subQ2=sQuery(id+"F0.wireOp",EDGE,"E25.6");var subQ3=sQuery(id+"F0.wireOp",EDGE,"E25.5");var subQ4=sQuery(id+"F0.wireOp",EDGE,"E25.4");var subQ5=sQuery(id+"F0.wireOp",EDGE,"E25.0");var subQ6=sQuery(id+"F0.wireOp",EDGE,"E25.2");var subQ7=sQuery(id+"F0.wireOp",EDGE,"E25.3");Q4=makeQuery(id+"F8.boolean.opBoolean","INTERSECT",EDGE,{"derivedFrom":[makeQuery(id+"F5.boolean.opBoolean","SPLIT",FACE,{"disambiguationData":[TD([makeQuery(id+"F2.opExtrude","SWEPT_FACE",FACE,{"disambiguationData":[OSD([subQ5])]})])],"derivedFrom":makeQuery(id+"F3.boolean.opBoolean","COPY",FACE,{"derivedFrom":makeQuery(id+"F3.opExtrude","CAP_FACE",FACE,{"disambiguationData":[OSD([subQ5,subQ1,subQ6,subQ7,subQ4,subQ3,subQ2,subQ0])],"isStart":false})})}),makeQuery(id+"F8.opExtrude","SWEPT_FACE",FACE,{"disambiguationData":[OSD([sQuery(id+"F7.wireOp",EDGE,"E67")])]})]});}
            var Q5;
            Q5=makeQuery(id+"F8.boolean.opBoolean","INTERSECT",EDGE,{"disambiguationData":[OD(0.0)],"derivedFrom":[makeQuery(id+"F5.opExtrude","SWEPT_FACE",FACE,{"disambiguationData":[OSD([sQuery(id+"F4.wireOp",EDGE,"E30")])]}),makeQuery(id+"F8.opExtrude","SWEPT_FACE",FACE,{"disambiguationData":[OSD([sQuery(id+"F7.wireOp",EDGE,"E67")])]})]});
            fillet(context, id + "F14", {"entities" : qUnion([Q0, Q1, Q2, Q3, Q4, Q5]), "radius" : 3 * mm, "tangentPropagation" : true, "allowEdgeOverflow" : false});
        }
        {
            var Q0;
            Q0=makeQuery(id+"F1.opExtrude","CAP_EDGE",EDGE,{"disambiguationData":[OSD([sQuery(id+"F0.wireOp",EDGE,"E1.bottom")])],"isStart":false});
            fillet(context, id + "F15", {"entities" : qUnion([Q0]), "radius" : 2 * mm, "tangentPropagation" : true, "allowEdgeOverflow" : false});
        }
        {
            var Q0;
            {var subQ0=sQuery(id+"F0.wireOp",EDGE,"E21.filletArc");var subQ1=sQuery(id+"F0.wireOp",EDGE,"E7");var subQ2=sQuery(id+"F0.wireOp",EDGE,"E6");var subQ3=sQuery(id+"F0.wireOp",EDGE,"E5");var subQ4=sQuery(id+"F0.wireOp",EDGE,"E4");var subQ5=sQuery(id+"F0.wireOp",EDGE,"E22.filletArc");var subQ6=sQuery(id+"F0.wireOp",EDGE,"E1.bottom");var subQ7=sQuery(id+"F0.wireOp",EDGE,"E1.right");var subQ8=sQuery(id+"F0.wireOp",EDGE,"E1.top");var subQ9=sQuery(id+"F0.wireOp",EDGE,"E1.left");var subQ10=sQuery(id+"F0.wireOp",EDGE,"E23.filletArc");var subQ11=sQuery(id+"F0.wireOp",EDGE,"E24.filletArc");Q0=makeQuery(id+"F2.boolean.opBoolean","SPLIT",FACE,{"disambiguationData":[TD([makeQuery(id+"F1.opExtrude","SWEPT_FACE",FACE,{"disambiguationData":[OSD([subQ6])]})])],"derivedFrom":makeQuery(id+"F1.opExtrude","CAP_FACE",FACE,{"disambiguationData":[OSD([subQ6,subQ8,subQ9,subQ7,subQ4,subQ3,subQ2,subQ1,subQ0,subQ5,subQ10,subQ11])],"isStart":true})});}
            var sketch = newSketch(context, id + "F16", { "sketchPlane" : qUnion([Q0])});
            skLineSegment(sketch, "E79", {"start": v(0, 90) * mm, "end": v(0, 120) * mm, "construction": true});
            skCircle(sketch, "E80", {"center": v(0, 120) * mm, "radius": 6 * mm});
            skArc(sketch, "E81", {"start": v(-15, 120) * mm, "mid": v(0, 135) * mm, "end": v(15, 120) * mm});
            skLineSegment(sketch, "E82", {"start": v(-15, 120) * mm, "end": v(-15, 108) * mm});
            skLineSegment(sketch, "E83", {"start": v(15, 120) * mm, "end": v(15, 108) * mm});
            skLineSegment(sketch, "E84", {"start": v(15, 108) * mm, "end": v(33, 90) * mm});
            skLineSegment(sketch, "E85", {"start": v(-15, 108) * mm, "end": v(-33, 90) * mm});
            skLineSegment(sketch, "E86", {"start": v(-80, 0) * mm, "end": v(80, 0) * mm, "construction": true});
            skArc(sketch, "E87.MirrorCS", {"start": v(-15, -120) * mm, "mid": v(0, -135) * mm, "end": v(15, -120) * mm});
            skCircle(sketch, "E88.MirrorC", {"center": v(0, -120) * mm, "radius": 6 * mm});
            skLineSegment(sketch, "E89.MirrorCS", {"start": v(-15, -120) * mm, "end": v(-15, -108) * mm});
            skLineSegment(sketch, "E90.MirrorCS", {"start": v(15, -120) * mm, "end": v(15, -108) * mm});
            skLineSegment(sketch, "E91.MirrorCS", {"start": v(-15, -108) * mm, "end": v(-33, -90) * mm});
            skLineSegment(sketch, "E92.MirrorCS", {"start": v(15, -108) * mm, "end": v(33, -90) * mm});
            skLineSegment(sketch, "E93.MirrorCS", {"start": v(0, -90) * mm, "end": v(0, -120) * mm, "construction": true});
            skSolve(sketch);
        }
        {
            var Q0;
            Q0=makeQuery(id+"F16.imprint","IMPRINT",FACE,{"disambiguationData":[TD([[makeQuery(id+"F16.imprint","IMPRINT",EDGE,{"derivedFrom":makeQuery(id+"F1.opExtrude","CAP_EDGE",EDGE,{"disambiguationData":[OSD([sQuery(id+"F0.wireOp",EDGE,"E1.left")])],"isStart":true})}),-1.0]])]});
            var Q1;
            Q1=makeQuery(id+"F16.imprint","IMPRINT",FACE,{"disambiguationData":[TD([[makeQuery(id+"F16.imprint","IMPRINT",EDGE,{"derivedFrom":sQuery(id+"F16.wireOp",EDGE,"E80")}),-1.0]])]});
            var Q2;
            Q2=makeQuery(id+"F16.imprint","IMPRINT",FACE,{"disambiguationData":[TD([[makeQuery(id+"F16.imprint","IMPRINT",EDGE,{"derivedFrom":sQuery(id+"F16.wireOp",EDGE,"E87.MirrorCS")}),1.0]])]});
            var Q3;
            Q3=makeQuery(id+"F2.opExtrude","CAP_FACE",FACE,{"disambiguationData":[OSD([sQuery(id+"F0.wireOp",EDGE,"E12"),sQuery(id+"F0.wireOp",EDGE,"E13"),sQuery(id+"F0.wireOp",EDGE,"E14"),sQuery(id+"F0.wireOp",EDGE,"E15"),sQuery(id+"F0.wireOp",EDGE,"E17.filletArc"),sQuery(id+"F0.wireOp",EDGE,"E18.filletArc"),sQuery(id+"F0.wireOp",EDGE,"E19.filletArc"),sQuery(id+"F0.wireOp",EDGE,"E20.filletArc"),sQuery(id+"F0.wireOp",EDGE,"E25.0"),sQuery(id+"F0.wireOp",EDGE,"E25.1"),sQuery(id+"F0.wireOp",EDGE,"E25.2"),sQuery(id+"F0.wireOp",EDGE,"E25.3"),sQuery(id+"F0.wireOp",EDGE,"E25.4"),sQuery(id+"F0.wireOp",EDGE,"E25.5"),sQuery(id+"F0.wireOp",EDGE,"E25.6"),sQuery(id+"F0.wireOp",EDGE,"E25.7")])],"isStart":false});
            extrude(context, id + "F17", {"entities" : qUnion([Q0, Q1, Q2]), "operationType" : NewBodyOperationType.ADD, "endBound" : BoundingType.UP_TO_SURFACE, "depth" : 25 * mm, "endBoundEntityFace" : qUnion([Q3]), "offsetDistance" : 25 * mm});
        }
    });
